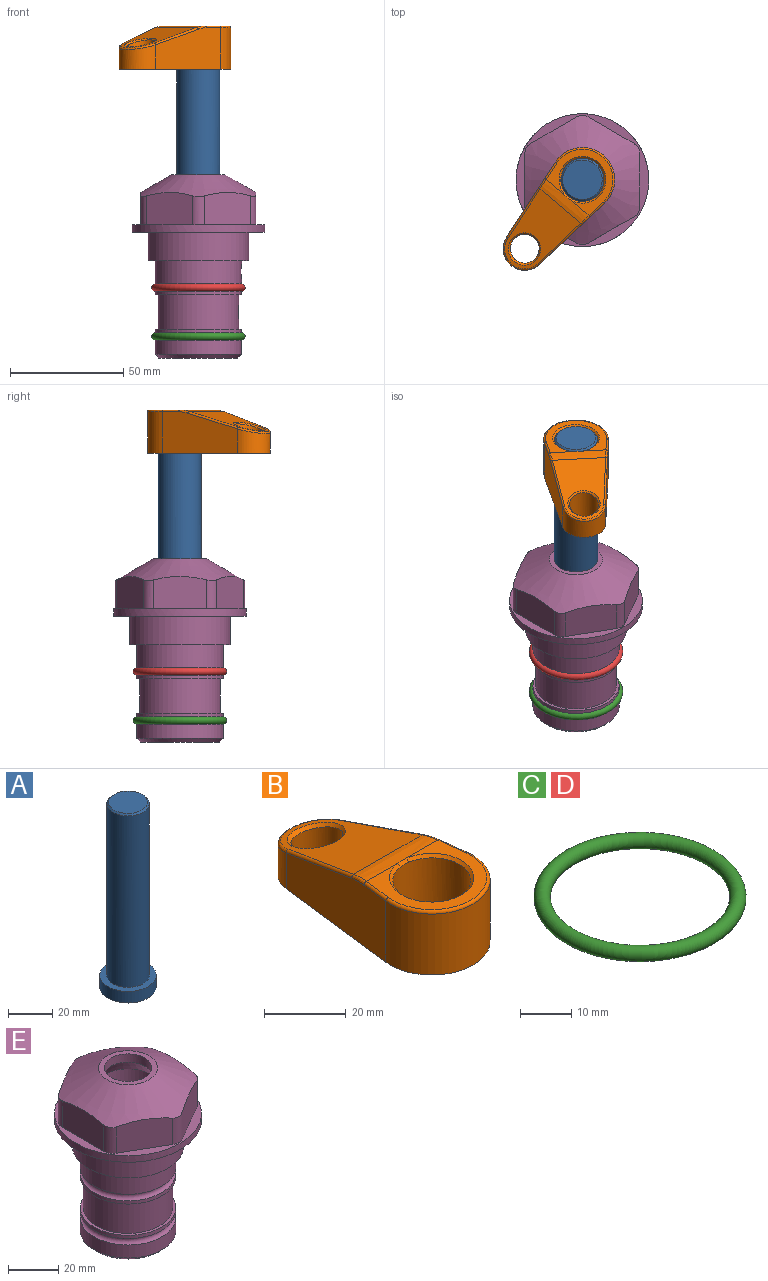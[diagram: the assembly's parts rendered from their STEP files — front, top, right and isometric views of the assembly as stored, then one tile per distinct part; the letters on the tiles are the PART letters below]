
ASSEMBLY  parts=5 mates=4
PART A: 6 faces, bbox 25.4x25.4x101.6 mm
  f0: plane 17.46x17.46mm, normal (0,0,1), area 239.5mm2, adj f5
  f1: plane 25.4x25.4mm, normal (0,0,-1), area 506.7mm2, adj f2
  f2: cylinder r=12.7mm len=25.4mm, axis (0,0,1), area 506.7mm2, adj f1,f3
  f3: plane 25.4x25.4mm, normal (0,0,1), area 221.7mm2, adj f2,f4
  f4: cylinder r=9.53mm len=94.46mm, axis (0,0,1), area 5653mm2, adj f3,f5
  f5: cone r=8.73mm half-angle=45deg, axis (0,0,-1), area 64.4mm2, adj f0,f4
PART B: 31 faces, bbox 31.7x65.5x19.8 mm
  f0: plane 39.12x18.26mm, normal (0.99,0.12,0), area 612.2mm2, adj f1,f4,f7,f11,f13,f15
  f1: cylinder r=9.53mm len=18.91mm, axis (0,0,-1), area 296.1mm2, adj f0,f2,f7,f17
  f2: plane 39.12x18.26mm, normal (-0.99,0.12,0), area 612.2mm2, adj f1,f4,f7,f12,f14,f16
  f3: cylinder r=6.35mm len=12.7mm, axis (0,0,-1), area 362.4mm2, adj f7,f18
  f4: cylinder r=14.29mm len=28.58mm, axis (0,0,-1), area 882.2mm2, adj f0,f2,f7,f10
  f5: cylinder r=9.53mm len=19.05mm, axis (0,0,-1), area 1092.6mm2, adj f7,f19,f20
  f6: plane 26.99x23.69mm, normal (0,0,1), area 216.2mm2, adj f9,f10,f11,f12,f19
  f7: plane 63.5x28.58mm, normal (0,0,-1), area 661.8mm2, adj f0,f1,f2,f3,f4,f5,f22,f23
  f8: plane 33.52x23.6mm, normal (0,0.26,0.97), area 486mm2, adj f9,f15,f16,f17,f18
  f9: cylinder r=19.05mm len=24.72mm, axis (1,0,0), area 120.4mm2, adj f6,f8,f13,f14,f20
  f10: torus R=13.49mm, axis (0,0,1), area 59mm2, adj f4,f6,f11,f12
  f11: cylinder r=0.79mm len=8.67mm, axis (0.12,-0.99,0), area 10.8mm2, adj f0,f6,f10,f13
  f12: cylinder r=0.79mm len=8.67mm, axis (0.12,0.99,0), area 10.8mm2, adj f2,f6,f10,f14
  f13: bspline ~4.95x1.42mm, area 6.1mm2, adj f0,f9,f11,f15
  f14: bspline ~4.95x1.42mm, area 6.1mm2, adj f2,f9,f12,f16
  f15: cylinder r=0.79mm len=25.95mm, axis (0.12,-0.96,0.26), area 32.9mm2, adj f0,f8,f13,f17
  f16: cylinder r=0.79mm len=25.95mm, axis (0.12,0.96,-0.26), area 32.9mm2, adj f2,f8,f14,f17
  f17: bspline ~18.91x8.38mm, area 30mm2, adj f1,f8,f15,f16
  f18: bspline ~14.29x14.29mm, area 48.3mm2, adj f3,f8
  f19: cone r=9.53mm half-angle=45deg, axis (0,0,1), area 66.5mm2, adj f5,f6,f20
  f20: bspline ~3.22x0.96mm, area 3.5mm2, adj f5,f9,f19
  f21: plane 2.75x2.72mm, normal (0,0,-1), area 2.9mm2, adj f23,f25,f28
  f22: plane 23.05x15.88mm, normal (-0.99,-0.12,0), area 323.6mm2, adj f7,f25,f26,f27,f28,f29
  f23: plane 23.05x15.88mm, normal (0.99,-0.12,0), area 323.6mm2, adj f7,f21,f25,f27,f28,f30
  f24: cylinder r=9.53mm len=10.69mm, axis (0,0,-1), area 114.7mm2, adj f7,f27,f29,f30
  f25: cylinder r=12.7mm len=20.59mm, axis (0,0,-1), area 381.1mm2, adj f7,f21,f22,f23,f26,f28
  f26: plane 2.75x2.72mm, normal (0,0,-1), area 2.9mm2, adj f22,f25,f28
  f27: plane 19.72x18.37mm, normal (0,-0.26,-0.97), area 291.8mm2, adj f22,f23,f24,f28,f29,f30
  f28: cylinder r=15.88mm len=19.92mm, axis (1,0,0), area 54.8mm2, adj f21,f22,f23,f25,f26,f27
  f29: cylinder r=1.59mm len=11mm, axis (0,0,-1), area 34.7mm2, adj f7,f22,f24,f27
  f30: cylinder r=1.59mm len=11mm, axis (0,0,-1), area 34.7mm2, adj f7,f23,f24,f27
PART C: 1 faces, bbox 44.7x44.7x3.2 mm
  f0: torus R=19.05mm, axis (0,0,1), area 1193.9mm2
PART D: same geometry as C
PART E: 36 faces, bbox 58.7x58.7x81 mm
  f0: cylinder r=17.78mm len=35.56mm, axis (0,0,1), area 1670.8mm2, adj f23,f24,f31
  f1: cylinder r=19.05mm len=38.1mm, axis (0,0,1), area 1191.9mm2, adj f26,f27,f30
  f2: plane 58.66x58.66mm, normal (0,0,-1), area 1150.6mm2, adj f3,f28
  f3: cylinder r=29.33mm len=58.66mm, axis (0,0,-1), area 585.1mm2, adj f2,f4
  f4: plane 58.66x58.66mm, normal (0,0,1), area 475.9mm2, adj f3,f5,f6,f7,f8,f9,f10,f11
  f5: plane 20.32x14.34mm, normal (-0.5,0.87,0), area 324.4mm2, adj f4,f15,f16,f17
  f6: plane 20.32x14.34mm, normal (0.5,0.87,0), area 324.4mm2, adj f4,f14,f15,f17
  f7: plane 23.48x14.34mm, normal (1,0,0), area 324.4mm2, adj f4,f13,f14,f17
  f8: plane 20.32x14.34mm, normal (0.5,-0.87,0), area 324.4mm2, adj f4,f12,f13,f17
  f9: plane 20.32x14.34mm, normal (-0.5,-0.87,0), area 324.4mm2, adj f4,f11,f12,f17
  f10: plane 23.48x14.34mm, normal (-1,0,0), area 324.4mm2, adj f4,f11,f16,f17
  f11: cylinder r=5.08mm len=12.85mm, axis (0,0,-1), area 67.2mm2, adj f4,f9,f10,f17
  f12: cylinder r=5.08mm len=12.85mm, axis (0,0,-1), area 67.2mm2, adj f4,f8,f9,f17
  f13: cylinder r=5.08mm len=12.85mm, axis (0,0,-1), area 67.2mm2, adj f4,f7,f8,f17
  f14: cylinder r=5.08mm len=12.85mm, axis (0,0,-1), area 67.2mm2, adj f4,f6,f7,f17
  f15: cylinder r=5.08mm len=12.85mm, axis (0,0,-1), area 67.2mm2, adj f4,f5,f6,f17
  f16: cylinder r=5.08mm len=12.85mm, axis (0,0,-1), area 67.2mm2, adj f4,f5,f10,f17
  f17: cone r=11.73mm half-angle=60deg, axis (0,0,-1), area 2071.8mm2, adj f5,f6,f7,f8,f9,f10,f11,f12
  f18: plane 23.46x23.46mm, normal (0,0,1), area 147.4mm2, adj f17,f35
  f19: plane 34.93x34.93mm, normal (0,0,-1), area 958mm2, adj f29
  f20: cylinder r=19.05mm len=38.1mm, axis (0,0,1), area 760.1mm2, adj f21,f29
  f21: torus R=19.05mm, axis (0,0,1), area 565.3mm2, adj f20,f22
  f22: cylinder r=19.05mm len=38.1mm, axis (0,0,1), area 190mm2, adj f21,f23
  f23: plane 38.1x38.1mm, normal (0,0,1), area 146.9mm2, adj f0,f22
  f24: plane 38.1x38.1mm, normal (0,0,-1), area 146.9mm2, adj f0,f25
  f25: cylinder r=19.05mm len=38.1mm, axis (0,0,1), area 190mm2, adj f24,f26
  f26: torus R=19.05mm, axis (0,0,1), area 565.3mm2, adj f1,f25
  f27: plane 44.45x44.45mm, normal (0,0,-1), area 411.7mm2, adj f1,f28
  f28: cylinder r=22.23mm len=44.45mm, axis (0,0,1), area 1773.5mm2, adj f2,f27
  f29: cone r=19.05mm half-angle=45deg, axis (0,0,1), area 257.5mm2, adj f19,f20
  f30: cylinder r=3.17mm len=6.75mm, axis (-1,0,0), area 128mm2, adj f1,f33
  f31: cylinder r=3.17mm len=6.35mm, axis (-1,0,0), area 102.5mm2, adj f0,f33
  f32: plane 25.4x25.4mm, normal (0,0,1), area 506.7mm2, adj f33
  f33: cylinder r=12.7mm len=66.42mm, axis (0,0,-1), area 5236.2mm2, adj f30,f31,f32,f34
  f34: cone r=9.53mm half-angle=30deg, axis (0,0,-1), area 443.4mm2, adj f33,f35
  f35: cylinder r=9.53mm len=19.05mm, axis (0,0,-1), area 240.9mm2, adj f18,f34
PLACE A rot(axis=(0,0,1),140.1deg) t=(0,0,27.55)mm
PLACE B rot(axis=(0,0,1),140.1deg) t=(0,0,27.55)mm
PLACE C t=(0,0,-21.59)mm
PLACE D at identity
PLACE E at identity fixed
MATE cylindrical A.f2 <-> E.f0  axis (0,0,-1) through (0,0,-10.55)mm
MATE fastened C.f0 <-> E.f0  axis (0,0,1) through (0,0,-46.1)mm
MATE fastened A.f2 <-> B.f4  axis (0,0,1) through (0,0,91.05)mm
MATE fastened D.f0 <-> E.f0  axis (0,0,1) through (0,0,-24.51)mm
